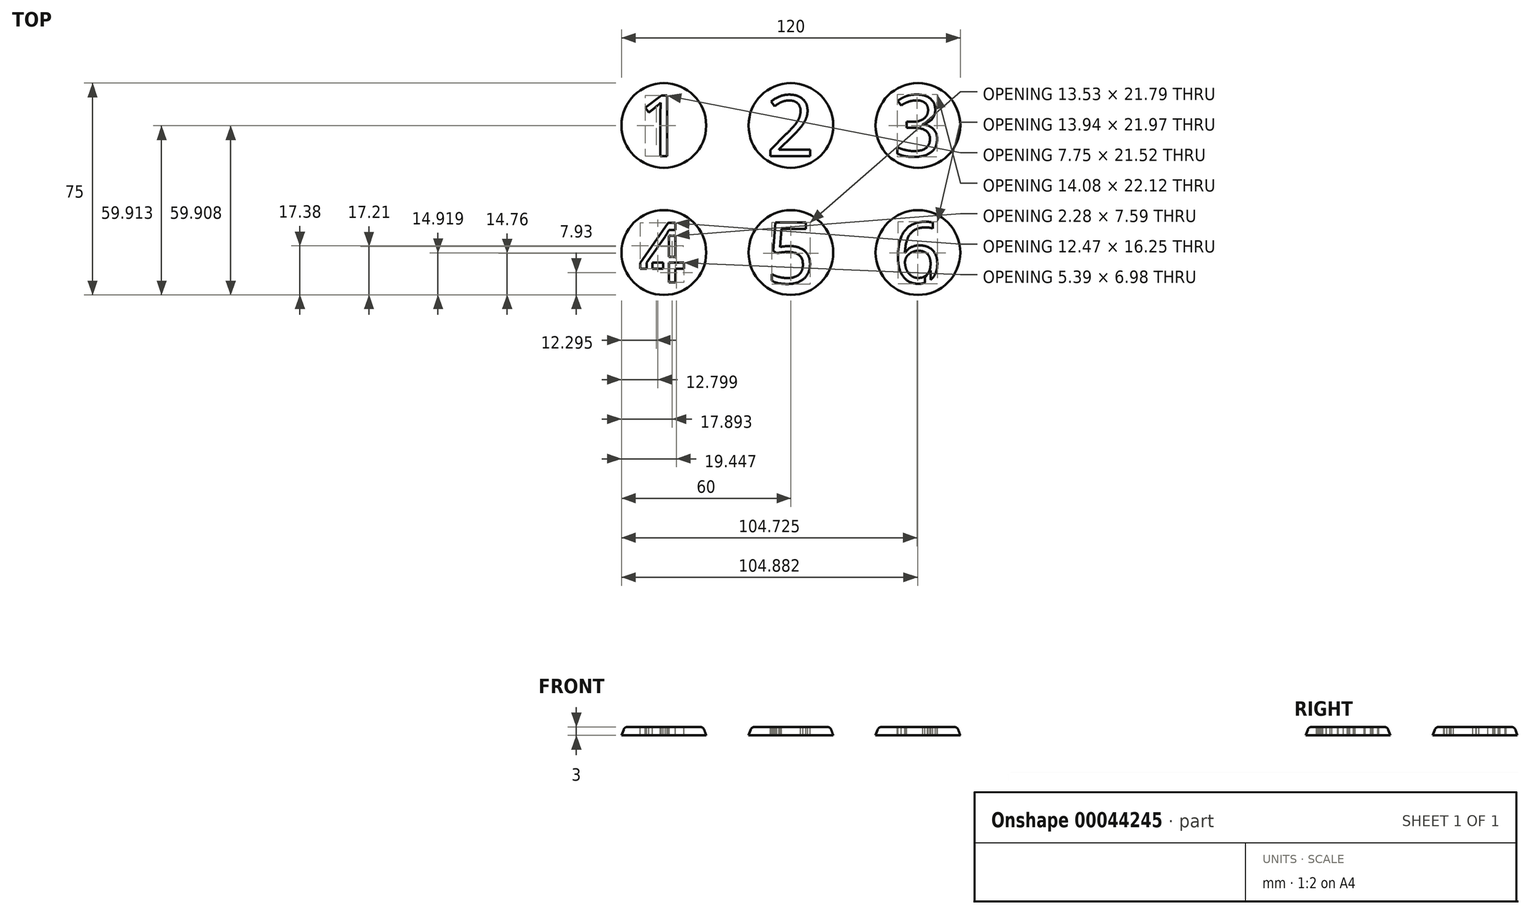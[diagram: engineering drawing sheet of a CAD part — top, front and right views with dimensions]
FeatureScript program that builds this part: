
annotation { "Feature Type Name" : "Feature", "Feature Type Description" : "" }
export const myFeature = defineFeature(function(context is Context, id is Id, definition is map)
    precondition{}
    {
        {
            var Q0;
            Q0=qCreatedBy(makeId("Top.planeOp"),FACE);
            var sketch = newSketch(context, id + "F0", { "sketchPlane" : qUnion([Q0])});
            skCircle(sketch, "E0", {"center": v(-45, 22.5) * mm, "radius": 15 * mm});
            skCircle(sketch, "E1.0.1.0", {"center": v(-45, -22.5) * mm, "radius": 15 * mm});
            skCircle(sketch, "E1.1.0.0", {"center": v(0, 22.5) * mm, "radius": 15 * mm});
            skCircle(sketch, "E1.1.1.0", {"center": v(0, -22.5) * mm, "radius": 15 * mm});
            skCircle(sketch, "E1.2.0.0", {"center": v(45, 22.5) * mm, "radius": 15 * mm});
            skCircle(sketch, "E1.2.1.0", {"center": v(45, -22.5) * mm, "radius": 15 * mm});
            skLineSegment(sketch, "E1.direction1", {"start": v(-45, 22.5) * mm, "end": v(0, 22.5) * mm, "construction": true});
            skLineSegment(sketch, "E1.direction2", {"start": v(-45, 22.5) * mm, "end": v(-45, -22.5) * mm, "construction": true});
            skPoint(sketch, "E2", {"position": v(-45, 0) * mm});
            skSolve(sketch);
        }
        {
            var Q0;
            Q0 = qSketchRegion(id + "F0", true);
            extrude(context, id + "F1", {"entities" : qUnion([Q0]), "depth" : 3 * mm, "hasDraft" : true, "draftAngle" : 20 * degree, "draftPullDirection" : true});
        }
        {
            var Q0;
            Q0=makeQuery(id+"F1.opExtrude","CAP_FACE",FACE,{"disambiguationData":[OSD([sQuery(id+"F0.wireOp",EDGE,"E0")])],"isStart":false});
            var sketch = newSketch(context, id + "F2", { "sketchPlane" : qUnion([Q0])});
            skCircle(sketch, "E3.0", {"center": v(-45, 22.5) * mm, "radius": 13.9 * mm});
            skCircle(sketch, "E4.0", {"center": v(0, 22.5) * mm, "radius": 13.9 * mm});
            skCircle(sketch, "E5.0", {"center": v(-45, -22.5) * mm, "radius": 13.9 * mm});
            skCircle(sketch, "E6.0", {"center": v(0, -22.5) * mm, "radius": 13.9 * mm});
            skCircle(sketch, "E7.0", {"center": v(45, -22.5) * mm, "radius": 13.9 * mm});
            skCircle(sketch, "E8.0", {"center": v(45, 22.5) * mm, "radius": 13.9 * mm});
            skText(sketch, "E9", { "text": "1", "fontName": "OpenSans-Regular.ttf"});
            skText(sketch, "E10", { "text": "2", "fontName": "OpenSans-Regular.ttf"});
            skText(sketch, "E11", { "text": "3", "fontName": "OpenSans-Regular.ttf"});
            skText(sketch, "E12", { "text": "4", "fontName": "OpenSans-Regular.ttf"});
            skText(sketch, "E13", { "text": "5", "fontName": "OpenSans-Regular.ttf"});
            skText(sketch, "E14", { "text": "6", "fontName": "OpenSans-Regular.ttf"});
            skCircle(sketch, "E15", {"center": v(-45, 22.5) * mm, "radius": 11.29 * mm});
            const initialGuessF2  = {"E9": [-0.05435, 0.01165, 1, 0, 0.0217], "E10": [-0.00875, 0.0117, 1, 0, 0.02162], "E11": [0.0363, 0.01165, 1, 0, 0.0217], "E12": [-0.05405, -0.03306, 1, 0, 0.02113], "E13": [-0.00872, -0.03334, 1, 0, 0.02168], "E14": [0.0362, -0.03327, 1, 0, 0.02155]};
            skSetInitialGuess(sketch, initialGuessF2);
            skSolve(sketch);
        }
        {
            var Q0;
            Q0=makeQuery(id+"F2.imprint","IMPRINT",FACE,{"disambiguationData":[TD([[makeQuery(id+"F2.imprint","IMPRINT",EDGE,{"derivedFrom":sQuery(id+"F2.wireOp",EDGE,"E9.sketch_text.stroke-0")}),-1.0]])]});
            var Q1;
            Q1=makeQuery(id+"F2.imprint","IMPRINT",FACE,{"disambiguationData":[TD([[makeQuery(id+"F2.imprint","IMPRINT",EDGE,{"derivedFrom":sQuery(id+"F2.wireOp",EDGE,"E10.sketch_text.stroke-0")}),-1.0]])]});
            var Q2;
            Q2=makeQuery(id+"F2.imprint","IMPRINT",FACE,{"disambiguationData":[TD([[makeQuery(id+"F2.imprint","IMPRINT",EDGE,{"derivedFrom":sQuery(id+"F2.wireOp",EDGE,"E11.sketch_text.stroke-0")}),-1.0]])]});
            var Q3;
            Q3=makeQuery(id+"F2.imprint","IMPRINT",FACE,{"disambiguationData":[TD([[makeQuery(id+"F2.imprint","IMPRINT",EDGE,{"derivedFrom":sQuery(id+"F2.wireOp",EDGE,"E12.sketch_text.stroke-0")}),-1.0]])]});
            var Q4;
            Q4=makeQuery(id+"F2.imprint","IMPRINT",FACE,{"disambiguationData":[TD([[makeQuery(id+"F2.imprint","IMPRINT",EDGE,{"derivedFrom":sQuery(id+"F2.wireOp",EDGE,"E14.sketch_text.stroke-0")}),-1.0]])]});
            var Q5;
            Q5=makeQuery(id+"F2.imprint","IMPRINT",FACE,{"disambiguationData":[TD([[makeQuery(id+"F2.imprint","IMPRINT",EDGE,{"derivedFrom":sQuery(id+"F2.wireOp",EDGE,"E13.sketch_text.stroke-0")}),-1.0]])]});
            extrude(context, id + "F3", {"entities" : qUnion([Q0, Q1, Q2, Q3, Q4, Q5]), "operationType" : NewBodyOperationType.REMOVE, "oppositeDirection" : true, "depth" : 25 * mm});
        }
        {
            var Q0;
            {var subQ0=sQuery(id+"F0.wireOp",EDGE,"E1.0.1.0");Q0=makeQuery(id+"F3.boolean.opBoolean","SPLIT",FACE,{"disambiguationData":[TD([makeQuery(id+"F1.opExtrude","SWEPT_FACE",FACE,{"disambiguationData":[OSD([subQ0])]})])],"derivedFrom":makeQuery(id+"F1.opExtrude","CAP_FACE",FACE,{"disambiguationData":[OSD([subQ0])],"isStart":false})});}
            var sketch = newSketch(context, id + "F4", { "sketchPlane" : qUnion([Q0])});
            skLineSegment(sketch, "E16", {"start": v(-43.24, -28.25) * mm, "end": v(-43.24, -26.09) * mm});
            skPoint(sketch, "E16.endSnap0", {"position": v(-43.24, -30.66) * mm});
            skLineSegment(sketch, "E17", {"start": v(-51.05, -28.25) * mm, "end": v(-51.05, -26.09) * mm});
            skLineSegment(sketch, "E18", {"start": v(-40.97, -14.5) * mm, "end": v(-43.21, -14.5) * mm});
            skLineSegment(sketch, "E19", {"start": v(-40.97, -16.5) * mm, "end": v(-43.2, -16.5) * mm});
            skLineSegment(sketch, "E20", {"start": v(-49.05, -28.25) * mm, "end": v(-49.05, -26.09) * mm});
            skLineSegment(sketch, "E21", {"start": v(-45.24, -28.25) * mm, "end": v(-45.24, -26.09) * mm});
            skLineSegment(sketch, "E22", {"start": v(-51.05, -26.09) * mm, "end": v(-49.05, -26.09) * mm});
            skLineSegment(sketch, "E23", {"start": v(-45.24, -26.09) * mm, "end": v(-43.24, -26.09) * mm});
            skLineSegment(sketch, "E24", {"start": v(-43.21, -14.5) * mm, "end": v(-43.2, -16.5) * mm});
            skLineSegment(sketch, "E25", {"start": v(-40.97, -14.5) * mm, "end": v(-40.97, -16.5) * mm});
            skLineSegment(sketch, "E26", {"start": v(-45.24, -28.25) * mm, "end": v(-43.24, -28.25) * mm});
            skLineSegment(sketch, "E27", {"start": v(-49.05, -28.25) * mm, "end": v(-51.05, -28.25) * mm});
            skLineSegment(sketch, "E28", {"start": v(-43.24, -26.09) * mm, "end": v(-40.97, -26.09) * mm});
            skLineSegment(sketch, "E29", {"start": v(-40.97, -26.09) * mm, "end": v(-40.97, -24.09) * mm});
            skLineSegment(sketch, "E30", {"start": v(-40.97, -24.09) * mm, "end": v(-43.24, -24.09) * mm});
            skLineSegment(sketch, "E31", {"start": v(-43.24, -24.09) * mm, "end": v(-43.24, -26.09) * mm});
            skSolve(sketch);
        }
        {
            var Q0;
            Q0 = qSketchRegion(id + "F4", true);
            extrude(context, id + "F5", {"entities" : qUnion([Q0]), "operationType" : NewBodyOperationType.ADD, "oppositeDirection" : true, "depth" : 3 * mm});
        }
        {
            var Q0;
            {var subQ0=sQuery(id+"F0.wireOp",EDGE,"E1.2.1.0");Q0=makeQuery(id+"F3.boolean.opBoolean","SPLIT",FACE,{"disambiguationData":[TD([makeQuery(id+"F1.opExtrude","SWEPT_FACE",FACE,{"disambiguationData":[OSD([subQ0])]})])],"derivedFrom":makeQuery(id+"F1.opExtrude","CAP_FACE",FACE,{"disambiguationData":[OSD([subQ0])],"isStart":false})});}
            var sketch = newSketch(context, id + "F6", { "sketchPlane" : qUnion([Q0])});
            skArc(sketch, "E32", {"start": v(40.4, -22.48) * mm, "mid": v(40.37, -24.33) * mm, "end": v(40.4, -26.2) * mm});
            skLineSegment(sketch, "E33", {"start": v(42.4, -20.72) * mm, "end": v(42.4, -22.63) * mm});
            skLineSegment(sketch, "E34", {"start": v(49.46, -32.2) * mm, "end": v(49.46, -26.42) * mm});
            skLineSegment(sketch, "E35", {"start": v(47.46, -33.24) * mm, "end": v(47.46, -30.92) * mm});
            skFitSpline(sketch, "E36.0", {"points": [v(48.31, -30.2) * mm, v(49.46, -28.89) * mm, v(49.46, -26.42) * mm]});
            skFitSpline(sketch, "E37.0", {"points": [v(45.09, -31.5) * mm, v(47.17, -31.5) * mm, v(48.31, -30.2) * mm]});
            skFitSpline(sketch, "E38.0", {"points": [v(50.04, -31.66) * mm, v(48.22, -33.57) * mm, v(45.12, -33.57) * mm]});
            skFitSpline(sketch, "E39.0", {"points": [v(40.57, -22.48) * mm, v(42.18, -19.96) * mm, v(45.66, -19.96) * mm]});
            skFitSpline(sketch, "E40.0", {"points": [v(42.8, -22.42) * mm, v(41.7, -22.96) * mm, v(41.05, -23.9) * mm]});
            skLineSegment(sketch, "E41.0", {"start": v(40.4, -22.48) * mm, "end": v(40.57, -22.48) * mm});
            skFitSpline(sketch, "E42.0", {"points": [v(40.4, -25.88) * mm, v(40.4, -27.39) * mm, v(40.98, -28.69) * mm]});
            skLineSegment(sketch, "E43", {"start": v(42.4, -22.63) * mm, "end": v(40.4, -26.2) * mm});
            skPoint(sketch, "E44.0.start.orphan", {"position": v(41.05, -23.9) * mm});
            skSolve(sketch);
        }
        {
            var Q0;
            {var subQ3=sQuery(id+"F6.wireOp",EDGE,"E34");Q0=makeQuery(id+"F6.imprint","IMPRINT",FACE,{"disambiguationData":[TD([[makeQuery(id+"F6.imprint","IMPRINT",EDGE,{"derivedFrom":subQ3}),1.0]])]});}
            var Q1;
            Q1=makeQuery(id+"F6.imprint","IMPRINT",FACE,{"disambiguationData":[TD([[makeQuery(id+"F6.imprint","IMPRINT",EDGE,{"derivedFrom":sQuery(id+"F6.wireOp",EDGE,"E32")}),1.0]])]});
            extrude(context, id + "F7", {"entities" : qUnion([Q0, Q1]), "operationType" : NewBodyOperationType.ADD, "oppositeDirection" : true, "depth" : 3 * mm});
        }
        {
            var Q0;
            Q0=makeQuery(id+"F1.opExtrude","CAP_EDGE",EDGE,{"disambiguationData":[OSD([sQuery(id+"F0.wireOp",EDGE,"E0")])],"isStart":false});
            var Q1;
            Q1=makeQuery(id+"F1.opExtrude","CAP_EDGE",EDGE,{"disambiguationData":[OSD([sQuery(id+"F0.wireOp",EDGE,"E1.1.0.0")])],"isStart":false});
            var Q2;
            Q2=makeQuery(id+"F1.opExtrude","CAP_EDGE",EDGE,{"disambiguationData":[OSD([sQuery(id+"F0.wireOp",EDGE,"E1.2.0.0")])],"isStart":false});
            var Q3;
            Q3=makeQuery(id+"F1.opExtrude","CAP_EDGE",EDGE,{"disambiguationData":[OSD([sQuery(id+"F0.wireOp",EDGE,"E1.0.1.0")])],"isStart":false});
            var Q4;
            Q4=makeQuery(id+"F1.opExtrude","CAP_EDGE",EDGE,{"disambiguationData":[OSD([sQuery(id+"F0.wireOp",EDGE,"E1.1.1.0")])],"isStart":false});
            var Q5;
            Q5=makeQuery(id+"F1.opExtrude","CAP_EDGE",EDGE,{"disambiguationData":[OSD([sQuery(id+"F0.wireOp",EDGE,"E1.2.1.0")])],"isStart":false});
            fillet(context, id + "F8", {"entities" : qUnion([Q0, Q1, Q2, Q3, Q4, Q5]), "radius" : 1.5 * mm, "tangentPropagation" : true, "allowEdgeOverflow" : false});
        }
    });
